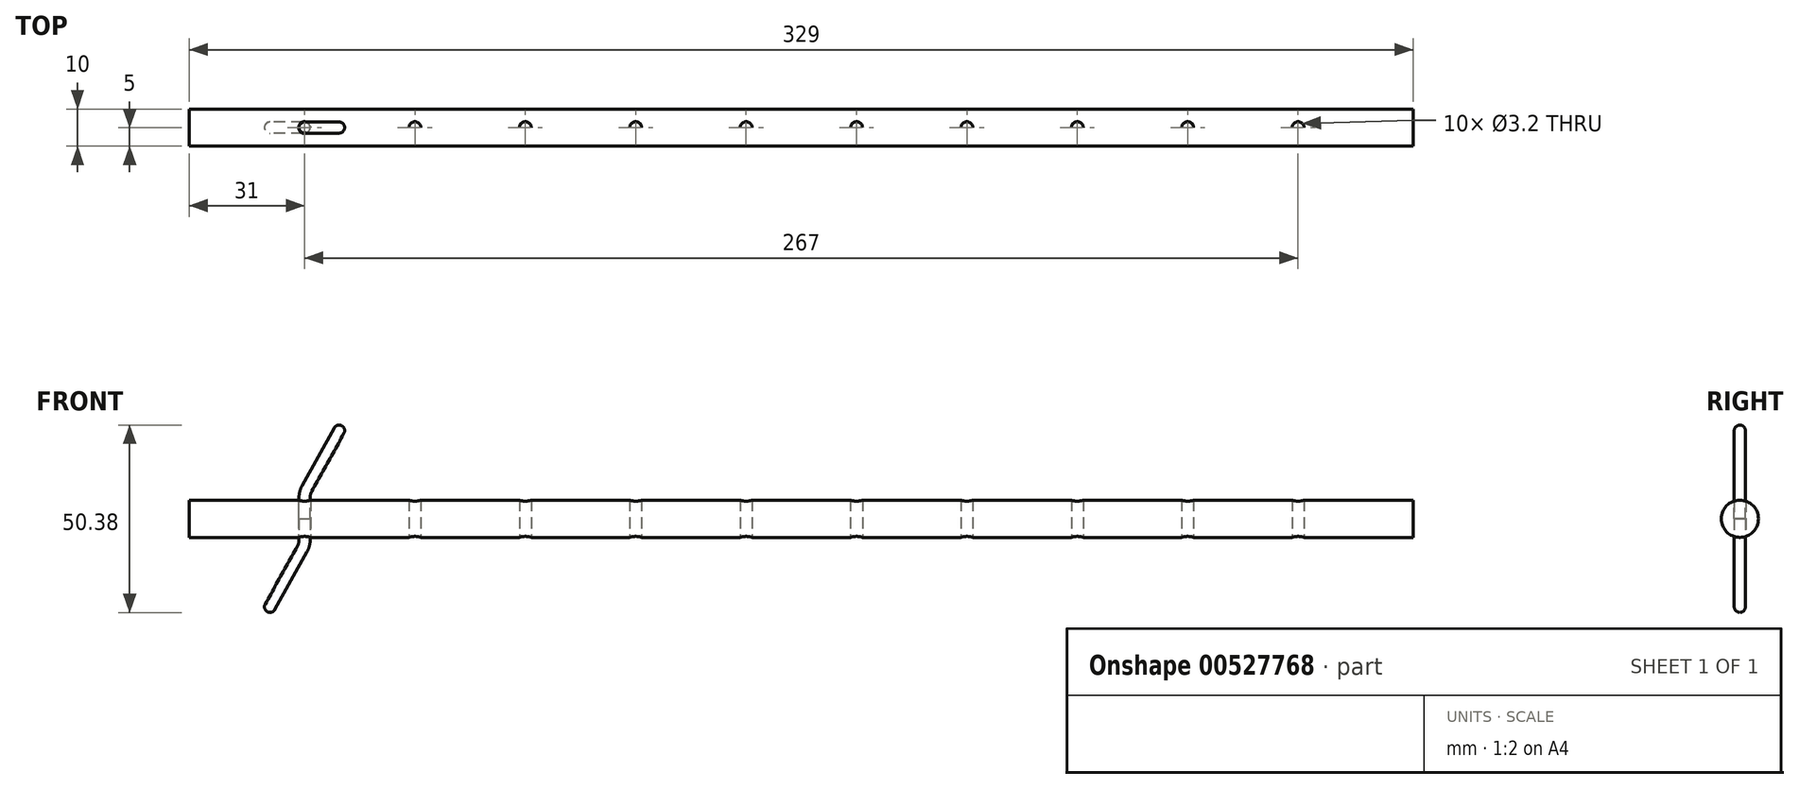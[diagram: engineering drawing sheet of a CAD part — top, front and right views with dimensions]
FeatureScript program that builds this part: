
annotation { "Feature Type Name" : "Feature", "Feature Type Description" : "" }
export const myFeature = defineFeature(function(context is Context, id is Id, definition is map)
    precondition{}
    {
        {
            var Q0;
            Q0=qCreatedBy(makeId("Right.planeOp"),FACE);
            var sketch = newSketch(context, id + "F0", { "sketchPlane" : qUnion([Q0])});
            skCircle(sketch, "E0", {"center": v(0, 0) * mm, "radius": 5 * mm});
            skSolve(sketch);
        }
        {
            var Q0;
            Q0 = qSketchRegion(id + "F0", true);
            extrude(context, id + "F1", {"entities" : qUnion([Q0]), "endBound" : BoundingType.SYMMETRIC, "depth" : 329 * mm, "offsetDistance" : 25 * mm});
        }
        {
            var Q0;
            Q0=qCreatedBy(makeId("Top.planeOp"),FACE);
            var sketch = newSketch(context, id + "F2", { "sketchPlane" : qUnion([Q0])});
            skLineSegment(sketch, "E1", {"start": v(0, 0) * mm, "end": v(0, 120.25) * mm, "construction": true});
            skLineSegment(sketch, "E2", {"start": v(148.5, 23.9) * mm, "end": v(148.5, -31.15) * mm, "construction": true});
            skLineSegment(sketch, "E3.MirrorCS", {"start": v(-148.5, 23.9) * mm, "end": v(-148.5, -31.15) * mm, "construction": true});
            skCircle(sketch, "E4", {"center": v(-133.5, 0) * mm, "radius": 1.6 * mm});
            skCircle(sketch, "E5.1.0.0", {"center": v(-103.83, 0) * mm, "radius": 1.6 * mm});
            skCircle(sketch, "E5.2.0.0", {"center": v(-74.17, 0) * mm, "radius": 1.6 * mm});
            skCircle(sketch, "E5.3.0.0", {"center": v(-44.5, 0) * mm, "radius": 1.6 * mm});
            skCircle(sketch, "E5.4.0.0", {"center": v(-14.83, 0) * mm, "radius": 1.6 * mm});
            skCircle(sketch, "E5.5.0.0", {"center": v(14.83, 0) * mm, "radius": 1.6 * mm});
            skCircle(sketch, "E5.6.0.0", {"center": v(44.5, 0) * mm, "radius": 1.6 * mm});
            skCircle(sketch, "E5.7.0.0", {"center": v(74.17, 0) * mm, "radius": 1.6 * mm});
            skCircle(sketch, "E5.8.0.0", {"center": v(103.83, 0) * mm, "radius": 1.6 * mm});
            skCircle(sketch, "E5.9.0.0", {"center": v(133.5, 0) * mm, "radius": 1.6 * mm});
            skLineSegment(sketch, "E5.direction1", {"start": v(-133.5, 0) * mm, "end": v(-103.83, 0) * mm, "construction": true});
            skSolve(sketch);
        }
        {
            var Q0;
            Q0 = qSketchRegion(id + "F2", true);
            extrude(context, id + "F3", {"entities" : qUnion([Q0]), "operationType" : NewBodyOperationType.REMOVE, "endBound" : BoundingType.THROUGH_ALL, "depth" : 25 * mm, "offsetDistance" : 25 * mm, "hasSecondDirection" : true, "secondDirectionBound" : SecondDirectionBoundingType.THROUGH_ALL, "secondDirectionOppositeDirection" : true, "secondDirectionDepth" : 25 * mm});
        }
        {
            var Q0;
            Q0=qCreatedBy(makeId("Front.planeOp"),FACE);
            var sketch = newSketch(context, id + "F4", { "sketchPlane" : qUnion([Q0])});
            skLineSegment(sketch, "E6", {"start": v(-133.5, 0) * mm, "end": v(-133.5, -5.7) * mm});
            skLineSegment(sketch, "E7", {"start": v(-134.13, -8.13) * mm, "end": v(-143.5, -25) * mm});
            skPoint(sketch, "E8", {"position": v(-133.5, 0) * mm});
            skPoint(sketch, "E9.orphan", {"position": v(-133.5, 7) * mm});
            skLineSegment(sketch, "E10", {"start": v(0, 0) * mm, "end": v(-133.5, 0) * mm, "construction": true});
            skPoint(sketch, "E11.visualSharp", {"position": v(-133.5, -7) * mm});
            skArc(sketch, "E11.filletArc", {"start": v(-134.13, -8.13) * mm, "mid": v(-133.66, -6.96) * mm, "end": v(-133.5, -5.7) * mm});
            skSolve(sketch);
        }
        {
            var Q0;
            Q0=qCreatedBy(makeId("Top.planeOp"),FACE);
            var sketch = newSketch(context, id + "F5", { "sketchPlane" : qUnion([Q0])});
            skCircle(sketch, "E12", {"center": v(-133.5, 0) * mm, "radius": 1.5 * mm});
            skLineSegment(sketch, "E13", {"start": v(-133.5, 0) * mm, "end": v(-133.5, -1.5) * mm, "construction": true});
            skSolve(sketch);
        }
        {
            var Q0;
            Q0 = qSketchRegion(id + "F5", true);
            var Q1;
            Q1 = qConstructionFilter(qBodyType(qCreatedBy(id + "F4" ,EDGE), BodyType.WIRE), ConstructionObject.NO);
            sweep(context, id + "F6", {"operationType" : NewBodyOperationType.ADD, "profiles" : qUnion([Q0]), "path" : qUnion([Q1])});
        }
        {
            var Q0;
            Q0=makeQuery(id+"F6.opSweep","CAP_EDGE",EDGE,{"disambiguationData":[OSD([sQuery(id+"F4.wireOp",VERTEX,"E7.end"),sQuery(id+"F5.wireOp",EDGE,"E12")])],"isStart":false});
            fillet(context, id + "F7", {"entities" : qUnion([Q0]), "radius" : (3 / 2) * mm, "allowEdgeOverflow" : false});
        }
        {
            var Q0;
            Q0=makeQuery(id+"F6.opSweep","SWEPT_BODY",BODY,{"disambiguationData":[OSD([sQuery(id+"F4.wireOp",EDGE,"E6"),sQuery(id+"F5.wireOp",EDGE,"E12")])]});
            var Q1;
            Q1=sQuery(id+"F5.wireOp",EDGE,"E13");
            circularPattern(context, id + "F8", {"entities" : qUnion([Q0]), "axis" : qUnion([Q1]), "angle" : 360 * degree, "instanceCount" : 2, "equalSpace" : true});
        }
    });
